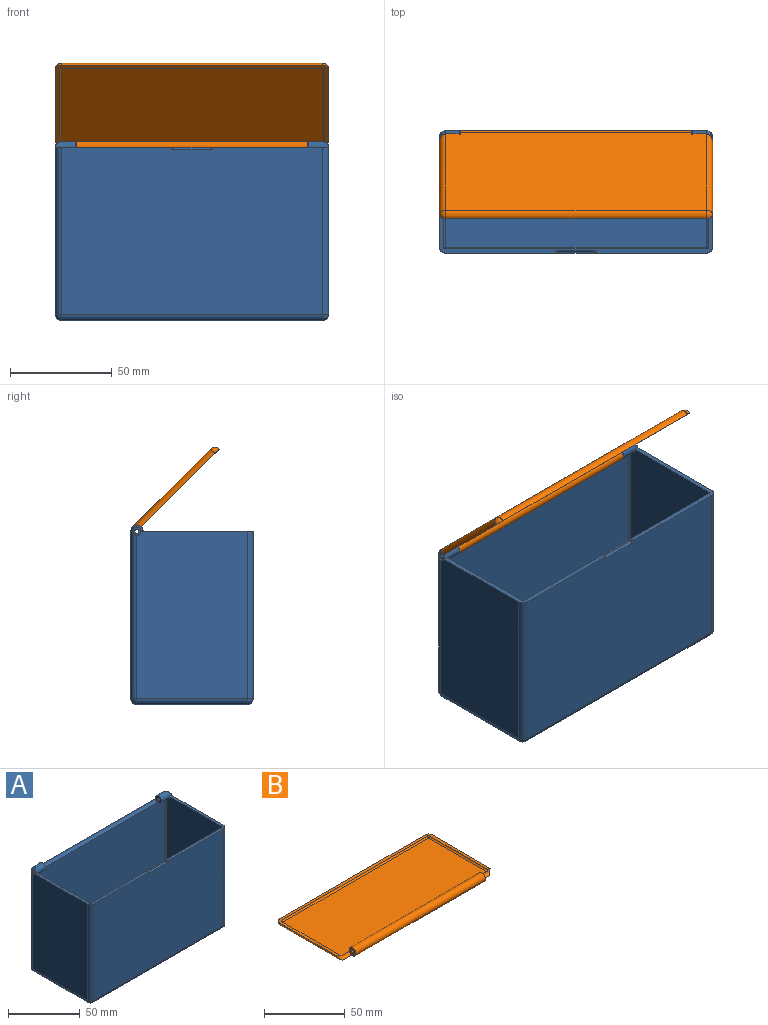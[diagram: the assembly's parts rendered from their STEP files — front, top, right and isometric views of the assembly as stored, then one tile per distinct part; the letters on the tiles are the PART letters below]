
ASSEMBLY  parts=2 mates=1
PART A: 53 faces, bbox 134x60x88 mm
  f0: plane 128x82mm, normal (0,-1,0), area 10476.4mm2, adj f1,f12,f13,f19,f50,f51,f52
  f1: plane 134x54mm, normal (0,0,1), area 453mm2, adj f0,f6,f9,f11,f12,f13,f23,f29
  f2: cylinder r=3mm len=82mm, axis (0,0,-1), area 383.1mm2, adj f5,f9,f10,f16,f24
  f3: cylinder r=3mm len=82mm, axis (0,0,-1), area 383.1mm2, adj f7,f10,f11,f20,f25
  f4: cylinder r=3mm len=3mm, axis (0,-1,0), area 5.6mm2, adj f5,f6,f9,f24
  f5: sphere r=3mm, area 10.5mm2, adj f2,f4,f6,f24
  f6: cylinder r=3mm len=10mm, axis (1,0,0), area 120.6mm2, adj f1,f4,f5,f10,f28,f29,f30,f47
  f7: sphere r=3mm, area 10.5mm2, adj f3,f8,f23,f25
  f8: cylinder r=3mm len=3mm, axis (0,1,0), area 5.6mm2, adj f7,f11,f23,f25
  f9: plane 82x54mm, normal (1,0,0), area 4424.9mm2, adj f1,f2,f4,f13,f15,f24
  f10: plane 128x82mm, normal (0,1,0), area 10407mm2, adj f2,f3,f6,f18,f23,f45,f46,f47
  f11: plane 82x54mm, normal (-1,0,0), area 4424.9mm2, adj f1,f3,f8,f12,f22,f25
  f12: cylinder r=3mm len=82mm, axis (0,0,-1), area 386.4mm2, adj f0,f1,f11,f21
  f13: cylinder r=3mm len=82mm, axis (0,0,-1), area 386.4mm2, adj f0,f1,f9,f17
  f14: plane 128x54mm, normal (0,0,-1), area 6912mm2, adj f15,f18,f19,f22
  f15: cylinder r=3mm len=54mm, axis (0,1,0), area 254.5mm2, adj f9,f14,f16,f17
  f16: sphere r=3mm, area 14.1mm2, adj f2,f15,f18
  f17: sphere r=3mm, area 14.1mm2, adj f13,f15,f19
  f18: cylinder r=3mm len=128mm, axis (-1,0,0), area 603.2mm2, adj f10,f14,f16,f20
  f19: cylinder r=3mm len=128mm, axis (1,0,0), area 603.2mm2, adj f0,f14,f17,f21
  f20: sphere r=3mm, area 14.1mm2, adj f3,f18,f22
  f21: sphere r=3mm, area 14.1mm2, adj f12,f19,f22
  f22: cylinder r=3mm len=54mm, axis (0,-1,0), area 254.5mm2, adj f11,f14,f20,f21
  f23: cylinder r=3mm len=10mm, axis (1,0,0), area 120.6mm2, adj f1,f7,f8,f10,f28,f31,f32,f46
  f24: cylinder r=2mm len=4mm, axis (1,0,0), area 7.9mm2, adj f2,f4,f5,f9,f48
  f25: cylinder r=2mm len=4mm, axis (1,0,0), area 7.9mm2, adj f3,f7,f8,f11,f49
  f26: cylinder r=1mm len=9mm, axis (1,0,0), area 56.5mm2, adj f46,f49
  f27: cylinder r=1mm len=9mm, axis (1,0,0), area 56.5mm2, adj f47,f48
  f28: plane 128x79.17mm, normal (0,-1,0), area 10121.9mm2, adj f6,f23,f30,f31,f44,f45,f46,f47
  f29: plane 82x54mm, normal (-1,0,0), area 4420.9mm2, adj f1,f6,f30,f35,f41
  f30: cylinder r=1mm len=79.17mm, axis (0,0,-1), area 124.2mm2, adj f6,f28,f29,f43
  f31: cylinder r=1mm len=79.17mm, axis (0,0,-1), area 124.2mm2, adj f23,f28,f32,f42
  f32: plane 82x54mm, normal (1,0,0), area 4420.9mm2, adj f1,f23,f31,f33,f40
  f33: cylinder r=1mm len=82mm, axis (0,0,-1), area 128.8mm2, adj f1,f32,f34,f38
  f34: plane 128x82mm, normal (0,1,0), area 10496mm2, adj f1,f33,f35,f37
  f35: cylinder r=1mm len=82mm, axis (0,0,-1), area 128.8mm2, adj f1,f29,f34,f39
  f36: plane 128x54mm, normal (0,0,1), area 6912mm2, adj f37,f40,f41,f44
  f37: cylinder r=1mm len=128mm, axis (1,0,0), area 201.1mm2, adj f34,f36,f38,f39
  f38: sphere r=1mm, area 1.6mm2, adj f33,f37,f40
  f39: sphere r=1mm, area 1.6mm2, adj f35,f37,f41
  f40: cylinder r=1mm len=54mm, axis (0,-1,0), area 84.8mm2, adj f32,f36,f38,f42
  f41: cylinder r=1mm len=54mm, axis (0,1,0), area 84.8mm2, adj f29,f36,f39,f43
  f42: sphere r=1mm, area 1.6mm2, adj f31,f40,f44
  f43: sphere r=1mm, area 1.6mm2, adj f30,f41,f44
  f44: cylinder r=1mm len=128mm, axis (-1,0,0), area 201.1mm2, adj f28,f36,f42,f43
  f45: cylinder r=3.1mm len=114mm, axis (1,0,0), area 349mm2, adj f10,f28,f46,f47
  f46: plane 6x6mm, normal (1,0,0), area 25.5mm2, adj f10,f23,f26,f28,f45
  f47: plane 6x6mm, normal (-1,0,0), area 25.5mm2, adj f6,f10,f27,f28,f45
  f48: plane 4x4mm, normal (1,0,0), area 9.4mm2, adj f24,f27
  f49: plane 4x4mm, normal (-1,0,0), area 9.4mm2, adj f25,f26
  f50: cylinder r=1mm len=18mm, axis (1,0,0), area 28.3mm2, adj f0,f1,f51,f52
  f51: sphere r=1mm, area 1.6mm2, adj f0,f1,f50
  f52: sphere r=1mm, area 1.6mm2, adj f0,f1,f50
PART B: 19 faces, bbox 134x60x6 mm
  f0: plane 134x53.9mm, normal (0,0,1), area 472.2mm2, adj f3,f4,f5,f6,f7,f9,f10,f11
  f1: cylinder r=3mm len=113.6mm, axis (1,0,0), area 1721.8mm2, adj f2,f8,f14,f16
  f2: plane 128x54mm, normal (0,0,-1), area 6900.8mm2, adj f1,f3,f4,f7,f14,f15,f16,f17
  f3: cylinder r=3mm len=53.22mm, axis (0,-1,0), area 244.5mm2, adj f0,f2,f5,f17
  f4: cylinder r=3mm len=53.22mm, axis (0,1,0), area 244.5mm2, adj f0,f2,f6,f15
  f5: sphere r=3mm, area 14.1mm2, adj f0,f3,f7
  f6: sphere r=3mm, area 14.1mm2, adj f0,f4,f7
  f7: cylinder r=3mm len=128mm, axis (-1,0,0), area 603.2mm2, adj f0,f2,f5,f6
  f8: plane 128x51.17mm, normal (0,0,1), area 6548.4mm2, adj f1,f9,f10,f13,f14,f15,f16,f17
  f9: cylinder r=1mm len=51.07mm, axis (0,-1,0), area 80.1mm2, adj f0,f8,f11,f17
  f10: cylinder r=1mm len=51.07mm, axis (0,1,0), area 80.1mm2, adj f0,f8,f12,f15
  f11: sphere r=1mm, area 1.6mm2, adj f0,f9,f13
  f12: sphere r=1mm, area 1.6mm2, adj f0,f10,f13
  f13: cylinder r=1mm len=128mm, axis (-1,0,0), area 201.1mm2, adj f0,f8,f11,f12
  f14: plane 6x6mm, normal (1,0,0), area 24.1mm2, adj f1,f2,f8,f15,f18
  f15: cylinder r=3.1mm len=10.2mm, axis (1,0,0), area 29.9mm2, adj f0,f2,f4,f8,f10,f14
  f16: plane 6x6mm, normal (-1,0,0), area 24.1mm2, adj f1,f2,f8,f17,f18
  f17: cylinder r=3.1mm len=10.2mm, axis (1,0,0), area 29.9mm2, adj f0,f2,f3,f8,f9,f16
  f18: cylinder r=1.2mm len=113.6mm, axis (1,0,0), area 856.5mm2, adj f14,f16
PLACE A t=(0,-252.59,-83.59)mm
PLACE B rot(axis=(1,0,0),135deg) t=(0,-180.89,26.08)mm
MATE revolute B.f1 <-> A.f6  axis (1,0,0) through (73.8,-160.47,1.41)mm
